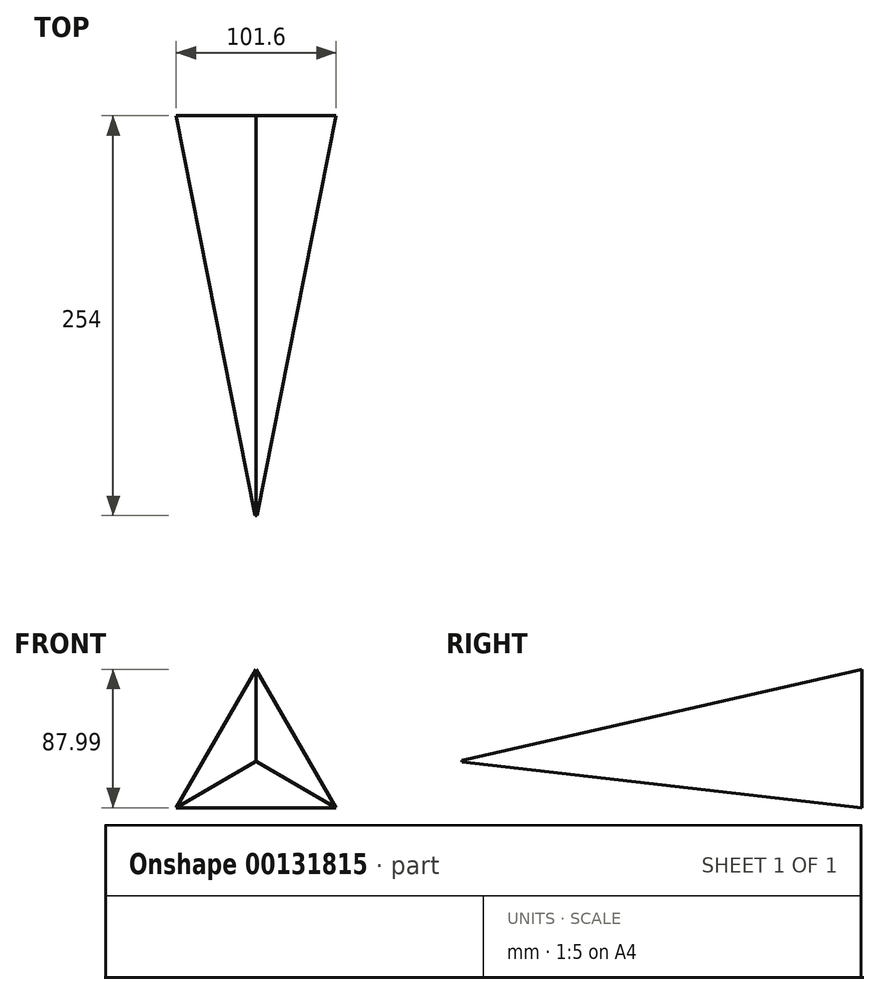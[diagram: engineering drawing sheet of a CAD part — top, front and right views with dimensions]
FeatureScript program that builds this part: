
annotation { "Feature Type Name" : "Feature", "Feature Type Description" : "" }
export const myFeature = defineFeature(function(context is Context, id is Id, definition is map)
    precondition{}
    {
        {
            var Q0;
            Q0=qCreatedBy(makeId("Front.planeOp"),FACE);
            var sketch = newSketch(context, id + "F0", { "sketchPlane" : qUnion([Q0])});
            skLineSegment(sketch, "E0", {"start": v(0, 0) * mm, "end": v(50.8, 0) * mm});
            skLineSegment(sketch, "E1", {"start": v(50.8, 0) * mm, "end": v(-50.8, 0) * mm});
            skLineSegment(sketch, "E2", {"start": v(-50.8, 0) * mm, "end": v(0, 87.99) * mm});
            skLineSegment(sketch, "E3", {"start": v(0, 87.99) * mm, "end": v(50.8, 0) * mm});
            skSolve(sketch);
        }
        {
            var Q0;
            {var subQ2=sQuery(id+"F0.wireOp",EDGE,"E2");Q0=makeQuery(id+"F0.imprint","IMPRINT",FACE,{"disambiguationData":[TD([[makeQuery(id+"F0.imprint","IMPRINT",EDGE,{"derivedFrom":subQ2}),-1.0]])]});}
            extrude(context, id + "F1", {"entities" : qUnion([Q0]), "depth" : 254 * mm, "hasDraft" : true, "draftAngle" : 6.5 * degree, "draftPullDirection" : true});
        }
    });
